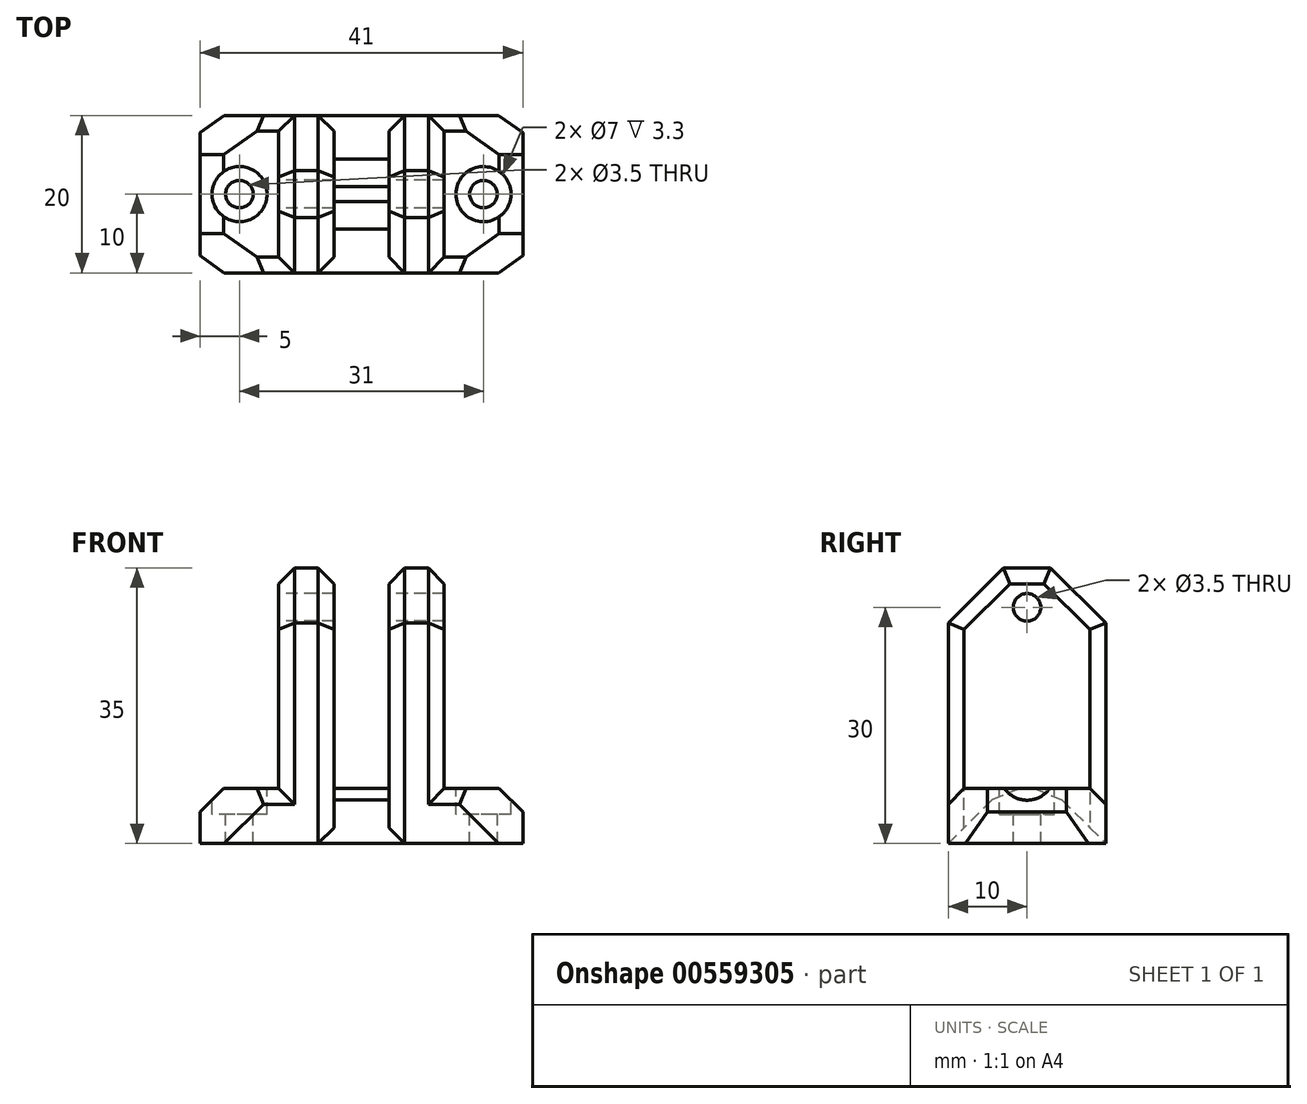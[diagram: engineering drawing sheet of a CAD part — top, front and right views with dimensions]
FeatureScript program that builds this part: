
annotation { "Feature Type Name" : "Feature", "Feature Type Description" : "" }
export const myFeature = defineFeature(function(context is Context, id is Id, definition is map)
    precondition{}
    {
        {
            var Q0;
            Q0=qCreatedBy(makeId("Front.planeOp"),FACE);
            var sketch = newSketch(context, id + "F0", { "sketchPlane" : qUnion([Q0])});
            skLineSegment(sketch, "E0", {"start": v(-20.5, 0) * mm, "end": v(20.5, 0) * mm});
            skLineSegment(sketch, "E1", {"start": v(0, 0) * mm, "end": v(0, 30) * mm, "construction": true});
            skLineSegment(sketch, "E2", {"start": v(0, 30) * mm, "end": v(0, 35) * mm, "construction": true});
            skLineSegment(sketch, "E3", {"start": v(0, 35) * mm, "end": v(3.5, 35) * mm, "construction": true});
            skLineSegment(sketch, "E4", {"start": v(0, 35) * mm, "end": v(-3.5, 35) * mm, "construction": true});
            skLineSegment(sketch, "E5", {"start": v(3.5, 35) * mm, "end": v(3.5, 0) * mm});
            skLineSegment(sketch, "E6", {"start": v(-3.5, 35) * mm, "end": v(-3.5, 0) * mm});
            skLineSegment(sketch, "E7", {"start": v(3.5, 35) * mm, "end": v(10.5, 35) * mm});
            skLineSegment(sketch, "E8", {"start": v(10.5, 35) * mm, "end": v(10.5, 0) * mm});
            skLineSegment(sketch, "E9", {"start": v(-3.5, 35) * mm, "end": v(-10.5, 35) * mm});
            skLineSegment(sketch, "E10", {"start": v(-10.5, 35) * mm, "end": v(-10.5, 0) * mm});
            skLineSegment(sketch, "E11", {"start": v(20.5, 0) * mm, "end": v(20.5, 7) * mm});
            skLineSegment(sketch, "E12", {"start": v(20.5, 7) * mm, "end": v(-20.5, 7) * mm});
            skLineSegment(sketch, "E13", {"start": v(-20.5, 7) * mm, "end": v(-20.5, 0) * mm});
            skSolve(sketch);
        }
        {
            var Q0;
            Q0 = qSketchRegion(id + "F0", true);
            extrude(context, id + "F1", {"entities" : qUnion([Q0]), "depth" : 20 * mm, "offsetDistance" : 25 * mm});
        }
        {
            var Q0;
            {var subQ0=sQuery(id+"F0.wireOp",EDGE,"E12");Q0=makeQuery(id+"F1.opExtrude","SWEPT_FACE",FACE,{"disambiguationData":[OSD([subQ0]),TDD([makeQuery(id+"F0.imprint","IMPRINT",EDGE,{"disambiguationData":[TD([[makeQuery(id+"F0.imprint","INTERSECT",VERTEX,{"derivedFrom":[sQuery(id+"F0.wireOp",EDGE,"E11"),subQ0]}),-1.0]])],"derivedFrom":subQ0})])]});}
            var sketch = newSketch(context, id + "F2", { "sketchPlane" : qUnion([Q0])});
            skLineSegment(sketch, "E14", {"start": v(20.5, -10) * mm, "end": v(15.5, -10) * mm});
            skCircle(sketch, "E15", {"center": v(15.5, -10) * mm, "radius": 3.5 * mm});
            skCircle(sketch, "E16", {"center": v(15.5, -10) * mm, "radius": 1.75 * mm});
            skSolve(sketch);
        }
        {
            var Q0;
            Q0 = qSketchRegion(id + "F2", true);
            extrude(context, id + "F3", {"entities" : qUnion([Q0]), "operationType" : NewBodyOperationType.REMOVE, "oppositeDirection" : true, "depth" : 3.3 * mm, "offsetDistance" : 25 * mm});
        }
        {
            var Q0;
            Q0=makeQuery(id+"F2.imprint","IMPRINT",FACE,{"disambiguationData":[TD([[makeQuery(id+"F2.imprint","IMPRINT",EDGE,{"derivedFrom":sQuery(id+"F2.wireOp",EDGE,"E16")}),1.0]])]});
            extrude(context, id + "F4", {"entities" : qUnion([Q0]), "operationType" : NewBodyOperationType.REMOVE, "oppositeDirection" : true, "depth" : 25 * mm, "offsetDistance" : 25 * mm});
        }
        {
            var Q0;
            {var subQ0=sQuery(id+"F0.wireOp",EDGE,"E12");Q0=makeQuery(id+"F1.opExtrude","SWEPT_FACE",FACE,{"disambiguationData":[OSD([subQ0]),TDD([makeQuery(id+"F0.imprint","IMPRINT",EDGE,{"disambiguationData":[TD([[makeQuery(id+"F0.imprint","INTERSECT",VERTEX,{"derivedFrom":[sQuery(id+"F0.wireOp",EDGE,"E10"),subQ0]}),-1.0]])],"derivedFrom":subQ0})])]});}
            var sketch = newSketch(context, id + "F5", { "sketchPlane" : qUnion([Q0])});
            skLineSegment(sketch, "E17", {"start": v(-20.5, -10) * mm, "end": v(-15.5, -10) * mm});
            skCircle(sketch, "E18", {"center": v(-15.5, -10) * mm, "radius": 3.5 * mm});
            skCircle(sketch, "E19", {"center": v(-15.5, -10) * mm, "radius": 1.75 * mm});
            skSolve(sketch);
        }
        {
            var Q0;
            Q0=makeQuery(id+"F5.imprint","IMPRINT",FACE,{"disambiguationData":[TD([[makeQuery(id+"F5.imprint","IMPRINT",EDGE,{"derivedFrom":sQuery(id+"F5.wireOp",EDGE,"E18")}),1.0]])]});
            extrude(context, id + "F6", {"entities" : qUnion([Q0]), "operationType" : NewBodyOperationType.REMOVE, "oppositeDirection" : true, "depth" : 3.3 * mm, "offsetDistance" : 25 * mm});
        }
        {
            var Q0;
            {var subQ0=sQuery(id+"F0.wireOp",EDGE,"E12");Q0=makeQuery(id+"F6.boolean.opBoolean","SPLIT",FACE,{"disambiguationData":[TD([makeQuery(id+"F6.opExtrude","SWEPT_FACE",FACE,{"disambiguationData":[OSD([sQuery(id+"F5.wireOp",EDGE,"E19")])]})])],"derivedFrom":makeQuery(id+"F1.opExtrude","SWEPT_FACE",FACE,{"disambiguationData":[OSD([subQ0]),TDD([makeQuery(id+"F0.imprint","IMPRINT",EDGE,{"disambiguationData":[TD([[makeQuery(id+"F0.imprint","INTERSECT",VERTEX,{"derivedFrom":[sQuery(id+"F0.wireOp",EDGE,"E10"),subQ0]}),-1.0]])],"derivedFrom":subQ0})])]})});}
            var Q1;
            Q1=sQuery(id+"F5.wireOp",EDGE,"E19");
            extrude(context, id + "F7", {"entities" : qUnion([Q0]), "operationType" : NewBodyOperationType.REMOVE, "surfaceEntities" : qUnion([Q1]), "oppositeDirection" : true, "depth" : 25 * mm, "offsetDistance" : 25 * mm});
        }
        {
            var Q0;
            Q0=makeQuery(id+"F1.opExtrude","SWEPT_FACE",FACE,{"disambiguationData":[OSD([sQuery(id+"F0.wireOp",EDGE,"E10")])]});
            var sketch = newSketch(context, id + "F8", { "sketchPlane" : qUnion([Q0])});
            skLineSegment(sketch, "E20", {"start": v(10, 35) * mm, "end": v(10, 30) * mm});
            skCircle(sketch, "E21", {"center": v(10, 30) * mm, "radius": 1.75 * mm});
            skSolve(sketch);
        }
        {
            var Q0;
            Q0 = qSketchRegion(id + "F8", true);
            extrude(context, id + "F9", {"entities" : qUnion([Q0]), "operationType" : NewBodyOperationType.REMOVE, "oppositeDirection" : true, "depth" : 25 * mm, "offsetDistance" : 25 * mm});
        }
        {
            var Q0;
            Q0=makeQuery(id+"F1.opExtrude","CAP_EDGE",EDGE,{"disambiguationData":[OSD([sQuery(id+"F0.wireOp",EDGE,"E9")])],"isStart":false});
            var Q1;
            Q1=makeQuery(id+"F1.opExtrude","CAP_EDGE",EDGE,{"disambiguationData":[OSD([sQuery(id+"F0.wireOp",EDGE,"E9")])],"isStart":true});
            var Q2;
            Q2=makeQuery(id+"F1.opExtrude","CAP_EDGE",EDGE,{"disambiguationData":[OSD([sQuery(id+"F0.wireOp",EDGE,"E7")])],"isStart":true});
            var Q3;
            Q3=makeQuery(id+"F1.opExtrude","CAP_EDGE",EDGE,{"disambiguationData":[OSD([sQuery(id+"F0.wireOp",EDGE,"E7")])],"isStart":false});
            chamfer(context, id + "F10", {"entities" : qUnion([Q0, Q1, Q2, Q3]), "width" : 7 * mm, "tangentPropagation" : true});
        }
        {
            var Q0;
            Q0=makeQuery(id+"F1.opExtrude","SWEPT_EDGE",EDGE,{"disambiguationData":[OSD([sQuery(id+"F0.wireOp",EDGE,"E11"),sQuery(id+"F0.wireOp",EDGE,"E12")])]});
            var Q1;
            Q1=makeQuery(id+"F1.opExtrude","SWEPT_EDGE",EDGE,{"disambiguationData":[OSD([sQuery(id+"F0.wireOp",EDGE,"E12"),sQuery(id+"F0.wireOp",EDGE,"E13")])]});
            chamfer(context, id + "F11", {"entities" : qUnion([Q0, Q1]), "width" : 3 * mm, "tangentPropagation" : true});
        }
        {
            var Q0;
            {var subQ0=sQuery(id+"F0.wireOp",EDGE,"E12");Q0=makeQuery(id+"F1.opExtrude","CAP_EDGE",EDGE,{"disambiguationData":[OSD([subQ0]),TDD([makeQuery(id+"F0.imprint","IMPRINT",EDGE,{"disambiguationData":[TD([[makeQuery(id+"F0.imprint","INTERSECT",VERTEX,{"derivedFrom":[sQuery(id+"F0.wireOp",EDGE,"E5"),subQ0]}),-1.0]])],"derivedFrom":subQ0})])],"isStart":true});}
            var Q1;
            {var subQ0=sQuery(id+"F0.wireOp",EDGE,"E12");Q1=makeQuery(id+"F1.opExtrude","CAP_EDGE",EDGE,{"disambiguationData":[OSD([subQ0]),TDD([makeQuery(id+"F0.imprint","IMPRINT",EDGE,{"disambiguationData":[TD([[makeQuery(id+"F0.imprint","INTERSECT",VERTEX,{"derivedFrom":[sQuery(id+"F0.wireOp",EDGE,"E5"),subQ0]}),-1.0]])],"derivedFrom":subQ0})])],"isStart":false});}
            chamfer(context, id + "F12", {"entities" : qUnion([Q0, Q1]), "width" : 7 * mm, "tangentPropagation" : true});
        }
        {
            var Q0;
            {var subQ0=sQuery(id+"F0.wireOp",EDGE,"E12");var subQ1=sQuery(id+"F0.wireOp",EDGE,"E11");Q0=makeQuery(id+"F11.opChamfer","BLEND_EDGE",EDGE,{"blendedFrom":[makeQuery(id+"F1.opExtrude","SWEPT_EDGE",EDGE,{"disambiguationData":[OSD([subQ1,subQ0])]}),makeQuery(id+"F1.opExtrude","CAP_FACE",FACE,{"disambiguationData":[OSD([sQuery(id+"F0.wireOp",EDGE,"E0"),sQuery(id+"F0.wireOp",EDGE,"E5"),sQuery(id+"F0.wireOp",EDGE,"E6"),sQuery(id+"F0.wireOp",EDGE,"E7"),sQuery(id+"F0.wireOp",EDGE,"E8"),sQuery(id+"F0.wireOp",EDGE,"E9"),sQuery(id+"F0.wireOp",EDGE,"E10"),subQ1,subQ0,sQuery(id+"F0.wireOp",EDGE,"E13")])],"isStart":false})],"blendedInto":[makeQuery(id+"F1.opExtrude","CAP_FACE",FACE,{"disambiguationData":[OSD([sQuery(id+"F0.wireOp",EDGE,"E0"),sQuery(id+"F0.wireOp",EDGE,"E5"),sQuery(id+"F0.wireOp",EDGE,"E6"),sQuery(id+"F0.wireOp",EDGE,"E7"),sQuery(id+"F0.wireOp",EDGE,"E8"),sQuery(id+"F0.wireOp",EDGE,"E9"),sQuery(id+"F0.wireOp",EDGE,"E10"),subQ1,subQ0,sQuery(id+"F0.wireOp",EDGE,"E13")])],"isStart":false})]});}
            var Q1;
            {var subQ0=sQuery(id+"F0.wireOp",EDGE,"E12");var subQ1=sQuery(id+"F0.wireOp",EDGE,"E11");Q1=makeQuery(id+"F11.opChamfer","BLEND_EDGE",EDGE,{"blendedFrom":[makeQuery(id+"F1.opExtrude","SWEPT_EDGE",EDGE,{"disambiguationData":[OSD([subQ1,subQ0])]}),makeQuery(id+"F1.opExtrude","CAP_FACE",FACE,{"disambiguationData":[OSD([sQuery(id+"F0.wireOp",EDGE,"E0"),sQuery(id+"F0.wireOp",EDGE,"E5"),sQuery(id+"F0.wireOp",EDGE,"E6"),sQuery(id+"F0.wireOp",EDGE,"E7"),sQuery(id+"F0.wireOp",EDGE,"E8"),sQuery(id+"F0.wireOp",EDGE,"E9"),sQuery(id+"F0.wireOp",EDGE,"E10"),subQ1,subQ0,sQuery(id+"F0.wireOp",EDGE,"E13")])],"isStart":true})],"blendedInto":[makeQuery(id+"F1.opExtrude","CAP_FACE",FACE,{"disambiguationData":[OSD([sQuery(id+"F0.wireOp",EDGE,"E0"),sQuery(id+"F0.wireOp",EDGE,"E5"),sQuery(id+"F0.wireOp",EDGE,"E6"),sQuery(id+"F0.wireOp",EDGE,"E7"),sQuery(id+"F0.wireOp",EDGE,"E8"),sQuery(id+"F0.wireOp",EDGE,"E9"),sQuery(id+"F0.wireOp",EDGE,"E10"),subQ1,subQ0,sQuery(id+"F0.wireOp",EDGE,"E13")])],"isStart":true})]});}
            var Q2;
            {var subQ0=sQuery(id+"F0.wireOp",EDGE,"E13");var subQ1=sQuery(id+"F0.wireOp",EDGE,"E12");Q2=makeQuery(id+"F11.opChamfer","BLEND_EDGE",EDGE,{"blendedFrom":[makeQuery(id+"F1.opExtrude","SWEPT_EDGE",EDGE,{"disambiguationData":[OSD([subQ1,subQ0])]}),makeQuery(id+"F1.opExtrude","CAP_FACE",FACE,{"disambiguationData":[OSD([sQuery(id+"F0.wireOp",EDGE,"E0"),sQuery(id+"F0.wireOp",EDGE,"E5"),sQuery(id+"F0.wireOp",EDGE,"E6"),sQuery(id+"F0.wireOp",EDGE,"E7"),sQuery(id+"F0.wireOp",EDGE,"E8"),sQuery(id+"F0.wireOp",EDGE,"E9"),sQuery(id+"F0.wireOp",EDGE,"E10"),sQuery(id+"F0.wireOp",EDGE,"E11"),subQ1,subQ0])],"isStart":true})],"blendedInto":[makeQuery(id+"F1.opExtrude","CAP_FACE",FACE,{"disambiguationData":[OSD([sQuery(id+"F0.wireOp",EDGE,"E0"),sQuery(id+"F0.wireOp",EDGE,"E5"),sQuery(id+"F0.wireOp",EDGE,"E6"),sQuery(id+"F0.wireOp",EDGE,"E7"),sQuery(id+"F0.wireOp",EDGE,"E8"),sQuery(id+"F0.wireOp",EDGE,"E9"),sQuery(id+"F0.wireOp",EDGE,"E10"),sQuery(id+"F0.wireOp",EDGE,"E11"),subQ1,subQ0])],"isStart":true})]});}
            var Q3;
            {var subQ0=sQuery(id+"F0.wireOp",EDGE,"E13");var subQ1=sQuery(id+"F0.wireOp",EDGE,"E12");Q3=makeQuery(id+"F11.opChamfer","BLEND_EDGE",EDGE,{"blendedFrom":[makeQuery(id+"F1.opExtrude","SWEPT_EDGE",EDGE,{"disambiguationData":[OSD([subQ1,subQ0])]}),makeQuery(id+"F1.opExtrude","CAP_FACE",FACE,{"disambiguationData":[OSD([sQuery(id+"F0.wireOp",EDGE,"E0"),sQuery(id+"F0.wireOp",EDGE,"E5"),sQuery(id+"F0.wireOp",EDGE,"E6"),sQuery(id+"F0.wireOp",EDGE,"E7"),sQuery(id+"F0.wireOp",EDGE,"E8"),sQuery(id+"F0.wireOp",EDGE,"E9"),sQuery(id+"F0.wireOp",EDGE,"E10"),sQuery(id+"F0.wireOp",EDGE,"E11"),subQ1,subQ0])],"isStart":false})],"blendedInto":[makeQuery(id+"F1.opExtrude","CAP_FACE",FACE,{"disambiguationData":[OSD([sQuery(id+"F0.wireOp",EDGE,"E0"),sQuery(id+"F0.wireOp",EDGE,"E5"),sQuery(id+"F0.wireOp",EDGE,"E6"),sQuery(id+"F0.wireOp",EDGE,"E7"),sQuery(id+"F0.wireOp",EDGE,"E8"),sQuery(id+"F0.wireOp",EDGE,"E9"),sQuery(id+"F0.wireOp",EDGE,"E10"),sQuery(id+"F0.wireOp",EDGE,"E11"),subQ1,subQ0])],"isStart":false})]});}
            var Q4;
            {var subQ0=sQuery(id+"F0.wireOp",EDGE,"E12");var subQ1=makeQuery(id+"F0.imprint","IMPRINT",EDGE,{"disambiguationData":[TD([[makeQuery(id+"F0.imprint","INTERSECT",VERTEX,{"derivedFrom":[sQuery(id+"F0.wireOp",EDGE,"E5"),subQ0]}),-1.0]])],"derivedFrom":subQ0});Q4=makeQuery(id+"F12.opChamfer","BLEND_EDGE",EDGE,{"blendedFrom":[makeQuery(id+"F1.opExtrude","CAP_EDGE",EDGE,{"disambiguationData":[OSD([subQ0]),TDD([subQ1])],"isStart":true}),makeQuery(id+"F1.opExtrude","SWEPT_FACE",FACE,{"disambiguationData":[OSD([subQ0]),TDD([subQ1])]})],"blendedInto":[makeQuery(id+"F1.opExtrude","SWEPT_FACE",FACE,{"disambiguationData":[OSD([subQ0]),TDD([subQ1])]})]});}
            var Q5;
            {var subQ0=sQuery(id+"F0.wireOp",EDGE,"E12");var subQ1=makeQuery(id+"F0.imprint","IMPRINT",EDGE,{"disambiguationData":[TD([[makeQuery(id+"F0.imprint","INTERSECT",VERTEX,{"derivedFrom":[sQuery(id+"F0.wireOp",EDGE,"E5"),subQ0]}),-1.0]])],"derivedFrom":subQ0});Q5=makeQuery(id+"F12.opChamfer","BLEND_EDGE",EDGE,{"blendedFrom":[makeQuery(id+"F1.opExtrude","CAP_EDGE",EDGE,{"disambiguationData":[OSD([subQ0]),TDD([subQ1])],"isStart":false}),makeQuery(id+"F1.opExtrude","SWEPT_FACE",FACE,{"disambiguationData":[OSD([subQ0]),TDD([subQ1])]})],"blendedInto":[makeQuery(id+"F1.opExtrude","SWEPT_FACE",FACE,{"disambiguationData":[OSD([subQ0]),TDD([subQ1])]})]});}
            chamfer(context, id + "F13", {"entities" : qUnion([Q0, Q1, Q2, Q3, Q4, Q5]), "width" : 5 * mm, "tangentPropagation" : true});
        }
        {
            var Q0;
            Q0=makeQuery(id+"F1.opExtrude","CAP_EDGE",EDGE,{"disambiguationData":[OSD([sQuery(id+"F0.wireOp",EDGE,"E10")])],"isStart":false});
            var Q1;
            Q1=makeQuery(id+"F1.opExtrude","CAP_EDGE",EDGE,{"disambiguationData":[OSD([sQuery(id+"F0.wireOp",EDGE,"E6")])],"isStart":false});
            var Q2;
            Q2=makeQuery(id+"F1.opExtrude","CAP_EDGE",EDGE,{"disambiguationData":[OSD([sQuery(id+"F0.wireOp",EDGE,"E5")])],"isStart":false});
            var Q3;
            Q3=makeQuery(id+"F1.opExtrude","CAP_EDGE",EDGE,{"disambiguationData":[OSD([sQuery(id+"F0.wireOp",EDGE,"E8")])],"isStart":false});
            var Q4;
            Q4=makeQuery(id+"F1.opExtrude","CAP_EDGE",EDGE,{"disambiguationData":[OSD([sQuery(id+"F0.wireOp",EDGE,"E8")])],"isStart":true});
            var Q5;
            Q5=makeQuery(id+"F1.opExtrude","CAP_EDGE",EDGE,{"disambiguationData":[OSD([sQuery(id+"F0.wireOp",EDGE,"E5")])],"isStart":true});
            var Q6;
            Q6=makeQuery(id+"F1.opExtrude","CAP_EDGE",EDGE,{"disambiguationData":[OSD([sQuery(id+"F0.wireOp",EDGE,"E6")])],"isStart":true});
            var Q7;
            Q7=makeQuery(id+"F1.opExtrude","CAP_EDGE",EDGE,{"disambiguationData":[OSD([sQuery(id+"F0.wireOp",EDGE,"E10")])],"isStart":true});
            var Q8;
            Q8=makeQuery(id+"F10.opChamfer","BLEND_EDGE",EDGE,{"blendedFrom":[makeQuery(id+"F1.opExtrude","CAP_EDGE",EDGE,{"disambiguationData":[OSD([sQuery(id+"F0.wireOp",EDGE,"E7")])],"isStart":false}),makeQuery(id+"F1.opExtrude","SWEPT_FACE",FACE,{"disambiguationData":[OSD([sQuery(id+"F0.wireOp",EDGE,"E8")])]})],"blendedInto":[makeQuery(id+"F1.opExtrude","SWEPT_FACE",FACE,{"disambiguationData":[OSD([sQuery(id+"F0.wireOp",EDGE,"E8")])]})]});
            var Q9;
            Q9=makeQuery(id+"F10.opChamfer","BLEND_EDGE",EDGE,{"blendedFrom":[makeQuery(id+"F1.opExtrude","CAP_EDGE",EDGE,{"disambiguationData":[OSD([sQuery(id+"F0.wireOp",EDGE,"E7")])],"isStart":false}),makeQuery(id+"F1.opExtrude","SWEPT_FACE",FACE,{"disambiguationData":[OSD([sQuery(id+"F0.wireOp",EDGE,"E5")])]})],"blendedInto":[makeQuery(id+"F1.opExtrude","SWEPT_FACE",FACE,{"disambiguationData":[OSD([sQuery(id+"F0.wireOp",EDGE,"E5")])]})]});
            var Q10;
            Q10=makeQuery(id+"F10.opChamfer","BLEND_EDGE",EDGE,{"blendedFrom":[makeQuery(id+"F1.opExtrude","CAP_EDGE",EDGE,{"disambiguationData":[OSD([sQuery(id+"F0.wireOp",EDGE,"E7")])],"isStart":true}),makeQuery(id+"F1.opExtrude","SWEPT_FACE",FACE,{"disambiguationData":[OSD([sQuery(id+"F0.wireOp",EDGE,"E5")])]})],"blendedInto":[makeQuery(id+"F1.opExtrude","SWEPT_FACE",FACE,{"disambiguationData":[OSD([sQuery(id+"F0.wireOp",EDGE,"E5")])]})]});
            var Q11;
            Q11=makeQuery(id+"F10.opChamfer","BLEND_EDGE",EDGE,{"blendedFrom":[makeQuery(id+"F1.opExtrude","CAP_EDGE",EDGE,{"disambiguationData":[OSD([sQuery(id+"F0.wireOp",EDGE,"E7")])],"isStart":true}),makeQuery(id+"F1.opExtrude","SWEPT_FACE",FACE,{"disambiguationData":[OSD([sQuery(id+"F0.wireOp",EDGE,"E8")])]})],"blendedInto":[makeQuery(id+"F1.opExtrude","SWEPT_FACE",FACE,{"disambiguationData":[OSD([sQuery(id+"F0.wireOp",EDGE,"E8")])]})]});
            var Q12;
            Q12=makeQuery(id+"F10.opChamfer","BLEND_EDGE",EDGE,{"blendedFrom":[makeQuery(id+"F1.opExtrude","CAP_EDGE",EDGE,{"disambiguationData":[OSD([sQuery(id+"F0.wireOp",EDGE,"E9")])],"isStart":false}),makeQuery(id+"F1.opExtrude","SWEPT_FACE",FACE,{"disambiguationData":[OSD([sQuery(id+"F0.wireOp",EDGE,"E10")])]})],"blendedInto":[makeQuery(id+"F1.opExtrude","SWEPT_FACE",FACE,{"disambiguationData":[OSD([sQuery(id+"F0.wireOp",EDGE,"E10")])]})]});
            var Q13;
            Q13=makeQuery(id+"F10.opChamfer","BLEND_EDGE",EDGE,{"blendedFrom":[makeQuery(id+"F1.opExtrude","CAP_EDGE",EDGE,{"disambiguationData":[OSD([sQuery(id+"F0.wireOp",EDGE,"E9")])],"isStart":false}),makeQuery(id+"F1.opExtrude","SWEPT_FACE",FACE,{"disambiguationData":[OSD([sQuery(id+"F0.wireOp",EDGE,"E6")])]})],"blendedInto":[makeQuery(id+"F1.opExtrude","SWEPT_FACE",FACE,{"disambiguationData":[OSD([sQuery(id+"F0.wireOp",EDGE,"E6")])]})]});
            var Q14;
            Q14=makeQuery(id+"F10.opChamfer","BLEND_EDGE",EDGE,{"blendedFrom":[makeQuery(id+"F1.opExtrude","CAP_EDGE",EDGE,{"disambiguationData":[OSD([sQuery(id+"F0.wireOp",EDGE,"E9")])],"isStart":true}),makeQuery(id+"F1.opExtrude","SWEPT_FACE",FACE,{"disambiguationData":[OSD([sQuery(id+"F0.wireOp",EDGE,"E6")])]})],"blendedInto":[makeQuery(id+"F1.opExtrude","SWEPT_FACE",FACE,{"disambiguationData":[OSD([sQuery(id+"F0.wireOp",EDGE,"E6")])]})]});
            var Q15;
            Q15=makeQuery(id+"F10.opChamfer","BLEND_EDGE",EDGE,{"blendedFrom":[makeQuery(id+"F1.opExtrude","CAP_EDGE",EDGE,{"disambiguationData":[OSD([sQuery(id+"F0.wireOp",EDGE,"E9")])],"isStart":true}),makeQuery(id+"F1.opExtrude","SWEPT_FACE",FACE,{"disambiguationData":[OSD([sQuery(id+"F0.wireOp",EDGE,"E10")])]})],"blendedInto":[makeQuery(id+"F1.opExtrude","SWEPT_FACE",FACE,{"disambiguationData":[OSD([sQuery(id+"F0.wireOp",EDGE,"E10")])]})]});
            chamfer(context, id + "F14", {"entities" : qUnion([Q0, Q1, Q2, Q3, Q4, Q5, Q6, Q7, Q8, Q9, Q10, Q11, Q12, Q13, Q14, Q15]), "width" : 2 * mm, "tangentPropagation" : true});
        }
        {
            var Q0;
            Q0=makeQuery(id+"F1.opExtrude","SWEPT_EDGE",EDGE,{"disambiguationData":[OSD([sQuery(id+"F0.wireOp",EDGE,"E7"),sQuery(id+"F0.wireOp",EDGE,"E8")])]});
            var Q1;
            Q1=makeQuery(id+"F1.opExtrude","SWEPT_EDGE",EDGE,{"disambiguationData":[OSD([sQuery(id+"F0.wireOp",EDGE,"E5"),sQuery(id+"F0.wireOp",EDGE,"E7")])]});
            var Q2;
            Q2=makeQuery(id+"F1.opExtrude","SWEPT_EDGE",EDGE,{"disambiguationData":[OSD([sQuery(id+"F0.wireOp",EDGE,"E6"),sQuery(id+"F0.wireOp",EDGE,"E9")])]});
            var Q3;
            Q3=makeQuery(id+"F1.opExtrude","SWEPT_EDGE",EDGE,{"disambiguationData":[OSD([sQuery(id+"F0.wireOp",EDGE,"E9"),sQuery(id+"F0.wireOp",EDGE,"E10")])]});
            chamfer(context, id + "F15", {"entities" : qUnion([Q0, Q1, Q2, Q3]), "width" : 2 * mm, "tangentPropagation" : true});
        }
        {
            var Q0;
            {var subQ0=sQuery(id+"F0.wireOp",EDGE,"E13");var subQ1=sQuery(id+"F0.wireOp",EDGE,"E12");var subQ2=sQuery(id+"F0.wireOp",EDGE,"E11");var subQ3=sQuery(id+"F0.wireOp",EDGE,"E10");var subQ4=sQuery(id+"F0.wireOp",EDGE,"E9");var subQ5=sQuery(id+"F0.wireOp",EDGE,"E8");var subQ6=sQuery(id+"F0.wireOp",EDGE,"E7");var subQ7=sQuery(id+"F0.wireOp",EDGE,"E6");var subQ8=sQuery(id+"F0.wireOp",EDGE,"E5");var subQ9=sQuery(id+"F0.wireOp",EDGE,"E0");var subQ10=makeQuery(id+"F1.opExtrude","CAP_FACE",FACE,{"disambiguationData":[OSD([subQ9,subQ8,subQ7,subQ6,subQ5,subQ4,subQ3,subQ2,subQ1,subQ0])],"isStart":false});var subQ11=subQ10;var subQ12=makeQuery(id+"F1.opExtrude","SWEPT_FACE",FACE,{"disambiguationData":[OSD([subQ3])]});var subQ13=subQ12;var subQ14=makeQuery(id+"F11.opChamfer","BLEND_EDGE",EDGE,{"blendedFrom":[makeQuery(id+"F1.opExtrude","SWEPT_EDGE",EDGE,{"disambiguationData":[OSD([subQ1,subQ0])]}),subQ11],"blendedInto":[subQ11]});Q0=makeQuery(id+"F14.opChamfer","TWEAK_EDGE",EDGE,{"derivedFrom":[makeQuery(id+"F13.opChamfer","BLEND_VERTEX",VERTEX,{"blendedFrom":[subQ14,subQ13,makeQuery(id+"F6.boolean.opBoolean","SPLIT",FACE,{"disambiguationData":[TD([subQ12])],"derivedFrom":makeQuery(id+"F1.opExtrude","SWEPT_FACE",FACE,{"disambiguationData":[OSD([subQ1]),TDD([makeQuery(id+"F0.imprint","IMPRINT",EDGE,{"disambiguationData":[TD([[makeQuery(id+"F0.imprint","INTERSECT",VERTEX,{"derivedFrom":[subQ3,subQ1]}),-1.0]])],"derivedFrom":subQ1})])]})})],"blendedInto":[subQ13,makeQuery(id+"F6.boolean.opBoolean","SPLIT",FACE,{"disambiguationData":[TD([subQ12])],"derivedFrom":makeQuery(id+"F1.opExtrude","SWEPT_FACE",FACE,{"disambiguationData":[OSD([subQ1]),TDD([makeQuery(id+"F0.imprint","IMPRINT",EDGE,{"disambiguationData":[TD([[makeQuery(id+"F0.imprint","INTERSECT",VERTEX,{"derivedFrom":[subQ3,subQ1]}),-1.0]])],"derivedFrom":subQ1})])]})})]}),makeQuery(id+"F13.opChamfer","BLEND_VERTEX",VERTEX,{"blendedFrom":[subQ14,subQ13,makeQuery(id+"F12.opChamfer","SPLIT",FACE,{"disambiguationData":[OD(1.0)],"derivedFrom":subQ11})],"blendedInto":[subQ13,makeQuery(id+"F12.opChamfer","SPLIT",FACE,{"disambiguationData":[OD(1.0)],"derivedFrom":subQ11})]})]});}
            var Q1;
            {var subQ0=sQuery(id+"F0.wireOp",EDGE,"E13");var subQ1=sQuery(id+"F0.wireOp",EDGE,"E12");var subQ2=sQuery(id+"F0.wireOp",EDGE,"E11");var subQ3=sQuery(id+"F0.wireOp",EDGE,"E10");var subQ4=sQuery(id+"F0.wireOp",EDGE,"E9");var subQ5=sQuery(id+"F0.wireOp",EDGE,"E8");var subQ6=sQuery(id+"F0.wireOp",EDGE,"E7");var subQ7=sQuery(id+"F0.wireOp",EDGE,"E6");var subQ8=sQuery(id+"F0.wireOp",EDGE,"E5");var subQ9=sQuery(id+"F0.wireOp",EDGE,"E0");var subQ10=makeQuery(id+"F1.opExtrude","CAP_FACE",FACE,{"disambiguationData":[OSD([subQ9,subQ8,subQ7,subQ6,subQ5,subQ4,subQ3,subQ2,subQ1,subQ0])],"isStart":false});var subQ11=subQ10;var subQ12=makeQuery(id+"F1.opExtrude","SWEPT_FACE",FACE,{"disambiguationData":[OSD([subQ5])]});var subQ13=subQ12;var subQ14=makeQuery(id+"F11.opChamfer","BLEND_EDGE",EDGE,{"blendedFrom":[makeQuery(id+"F1.opExtrude","SWEPT_EDGE",EDGE,{"disambiguationData":[OSD([subQ2,subQ1])]}),subQ11],"blendedInto":[subQ11]});Q1=makeQuery(id+"F14.opChamfer","TWEAK_EDGE",EDGE,{"derivedFrom":[makeQuery(id+"F13.opChamfer","BLEND_VERTEX",VERTEX,{"blendedFrom":[subQ14,subQ13,makeQuery(id+"F3.boolean.opBoolean","SPLIT",FACE,{"disambiguationData":[TD([subQ12])],"derivedFrom":makeQuery(id+"F1.opExtrude","SWEPT_FACE",FACE,{"disambiguationData":[OSD([subQ1]),TDD([makeQuery(id+"F0.imprint","IMPRINT",EDGE,{"disambiguationData":[TD([[makeQuery(id+"F0.imprint","INTERSECT",VERTEX,{"derivedFrom":[subQ2,subQ1]}),-1.0]])],"derivedFrom":subQ1})])]})})],"blendedInto":[subQ13,makeQuery(id+"F3.boolean.opBoolean","SPLIT",FACE,{"disambiguationData":[TD([subQ12])],"derivedFrom":makeQuery(id+"F1.opExtrude","SWEPT_FACE",FACE,{"disambiguationData":[OSD([subQ1]),TDD([makeQuery(id+"F0.imprint","IMPRINT",EDGE,{"disambiguationData":[TD([[makeQuery(id+"F0.imprint","INTERSECT",VERTEX,{"derivedFrom":[subQ2,subQ1]}),-1.0]])],"derivedFrom":subQ1})])]})})]}),makeQuery(id+"F13.opChamfer","BLEND_VERTEX",VERTEX,{"blendedFrom":[subQ14,subQ13,makeQuery(id+"F12.opChamfer","SPLIT",FACE,{"disambiguationData":[OD(0.0)],"derivedFrom":subQ11})],"blendedInto":[subQ13,makeQuery(id+"F12.opChamfer","SPLIT",FACE,{"disambiguationData":[OD(0.0)],"derivedFrom":subQ11})]})]});}
            var Q2;
            {var subQ0=sQuery(id+"F0.wireOp",EDGE,"E13");var subQ1=sQuery(id+"F0.wireOp",EDGE,"E12");var subQ2=sQuery(id+"F0.wireOp",EDGE,"E11");var subQ3=sQuery(id+"F0.wireOp",EDGE,"E10");var subQ4=sQuery(id+"F0.wireOp",EDGE,"E9");var subQ5=sQuery(id+"F0.wireOp",EDGE,"E8");var subQ6=sQuery(id+"F0.wireOp",EDGE,"E7");var subQ7=sQuery(id+"F0.wireOp",EDGE,"E6");var subQ8=sQuery(id+"F0.wireOp",EDGE,"E5");var subQ9=sQuery(id+"F0.wireOp",EDGE,"E0");var subQ10=makeQuery(id+"F1.opExtrude","CAP_FACE",FACE,{"disambiguationData":[OSD([subQ9,subQ8,subQ7,subQ6,subQ5,subQ4,subQ3,subQ2,subQ1,subQ0])],"isStart":true});var subQ11=subQ10;var subQ12=makeQuery(id+"F1.opExtrude","SWEPT_FACE",FACE,{"disambiguationData":[OSD([subQ5])]});var subQ13=subQ12;var subQ14=makeQuery(id+"F11.opChamfer","BLEND_EDGE",EDGE,{"blendedFrom":[makeQuery(id+"F1.opExtrude","SWEPT_EDGE",EDGE,{"disambiguationData":[OSD([subQ2,subQ1])]}),subQ11],"blendedInto":[subQ11]});Q2=makeQuery(id+"F14.opChamfer","TWEAK_EDGE",EDGE,{"derivedFrom":[makeQuery(id+"F13.opChamfer","BLEND_VERTEX",VERTEX,{"blendedFrom":[subQ14,subQ13,makeQuery(id+"F3.boolean.opBoolean","SPLIT",FACE,{"disambiguationData":[TD([subQ12])],"derivedFrom":makeQuery(id+"F1.opExtrude","SWEPT_FACE",FACE,{"disambiguationData":[OSD([subQ1]),TDD([makeQuery(id+"F0.imprint","IMPRINT",EDGE,{"disambiguationData":[TD([[makeQuery(id+"F0.imprint","INTERSECT",VERTEX,{"derivedFrom":[subQ2,subQ1]}),-1.0]])],"derivedFrom":subQ1})])]})})],"blendedInto":[subQ13,makeQuery(id+"F3.boolean.opBoolean","SPLIT",FACE,{"disambiguationData":[TD([subQ12])],"derivedFrom":makeQuery(id+"F1.opExtrude","SWEPT_FACE",FACE,{"disambiguationData":[OSD([subQ1]),TDD([makeQuery(id+"F0.imprint","IMPRINT",EDGE,{"disambiguationData":[TD([[makeQuery(id+"F0.imprint","INTERSECT",VERTEX,{"derivedFrom":[subQ2,subQ1]}),-1.0]])],"derivedFrom":subQ1})])]})})]}),makeQuery(id+"F13.opChamfer","BLEND_VERTEX",VERTEX,{"blendedFrom":[subQ14,subQ13,makeQuery(id+"F12.opChamfer","SPLIT",FACE,{"disambiguationData":[OD(0.0)],"derivedFrom":subQ11})],"blendedInto":[subQ13,makeQuery(id+"F12.opChamfer","SPLIT",FACE,{"disambiguationData":[OD(0.0)],"derivedFrom":subQ11})]})]});}
            var Q3;
            {var subQ0=sQuery(id+"F0.wireOp",EDGE,"E13");var subQ1=sQuery(id+"F0.wireOp",EDGE,"E12");var subQ2=sQuery(id+"F0.wireOp",EDGE,"E11");var subQ3=sQuery(id+"F0.wireOp",EDGE,"E10");var subQ4=sQuery(id+"F0.wireOp",EDGE,"E9");var subQ5=sQuery(id+"F0.wireOp",EDGE,"E8");var subQ6=sQuery(id+"F0.wireOp",EDGE,"E7");var subQ7=sQuery(id+"F0.wireOp",EDGE,"E6");var subQ8=sQuery(id+"F0.wireOp",EDGE,"E5");var subQ9=sQuery(id+"F0.wireOp",EDGE,"E0");var subQ10=makeQuery(id+"F1.opExtrude","CAP_FACE",FACE,{"disambiguationData":[OSD([subQ9,subQ8,subQ7,subQ6,subQ5,subQ4,subQ3,subQ2,subQ1,subQ0])],"isStart":true});var subQ11=subQ10;var subQ12=makeQuery(id+"F1.opExtrude","SWEPT_FACE",FACE,{"disambiguationData":[OSD([subQ3])]});var subQ13=subQ12;var subQ14=makeQuery(id+"F11.opChamfer","BLEND_EDGE",EDGE,{"blendedFrom":[makeQuery(id+"F1.opExtrude","SWEPT_EDGE",EDGE,{"disambiguationData":[OSD([subQ1,subQ0])]}),subQ11],"blendedInto":[subQ11]});Q3=makeQuery(id+"F14.opChamfer","TWEAK_EDGE",EDGE,{"derivedFrom":[makeQuery(id+"F13.opChamfer","BLEND_VERTEX",VERTEX,{"blendedFrom":[subQ14,subQ13,makeQuery(id+"F6.boolean.opBoolean","SPLIT",FACE,{"disambiguationData":[TD([subQ12])],"derivedFrom":makeQuery(id+"F1.opExtrude","SWEPT_FACE",FACE,{"disambiguationData":[OSD([subQ1]),TDD([makeQuery(id+"F0.imprint","IMPRINT",EDGE,{"disambiguationData":[TD([[makeQuery(id+"F0.imprint","INTERSECT",VERTEX,{"derivedFrom":[subQ3,subQ1]}),-1.0]])],"derivedFrom":subQ1})])]})})],"blendedInto":[subQ13,makeQuery(id+"F6.boolean.opBoolean","SPLIT",FACE,{"disambiguationData":[TD([subQ12])],"derivedFrom":makeQuery(id+"F1.opExtrude","SWEPT_FACE",FACE,{"disambiguationData":[OSD([subQ1]),TDD([makeQuery(id+"F0.imprint","IMPRINT",EDGE,{"disambiguationData":[TD([[makeQuery(id+"F0.imprint","INTERSECT",VERTEX,{"derivedFrom":[subQ3,subQ1]}),-1.0]])],"derivedFrom":subQ1})])]})})]}),makeQuery(id+"F13.opChamfer","BLEND_VERTEX",VERTEX,{"blendedFrom":[subQ14,subQ13,makeQuery(id+"F12.opChamfer","SPLIT",FACE,{"disambiguationData":[OD(1.0)],"derivedFrom":subQ11})],"blendedInto":[subQ13,makeQuery(id+"F12.opChamfer","SPLIT",FACE,{"disambiguationData":[OD(1.0)],"derivedFrom":subQ11})]})]});}
            chamfer(context, id + "F16", {"entities" : qUnion([Q0, Q1, Q2, Q3]), "width" : 2 * mm, "tangentPropagation" : true});
        }
    });
